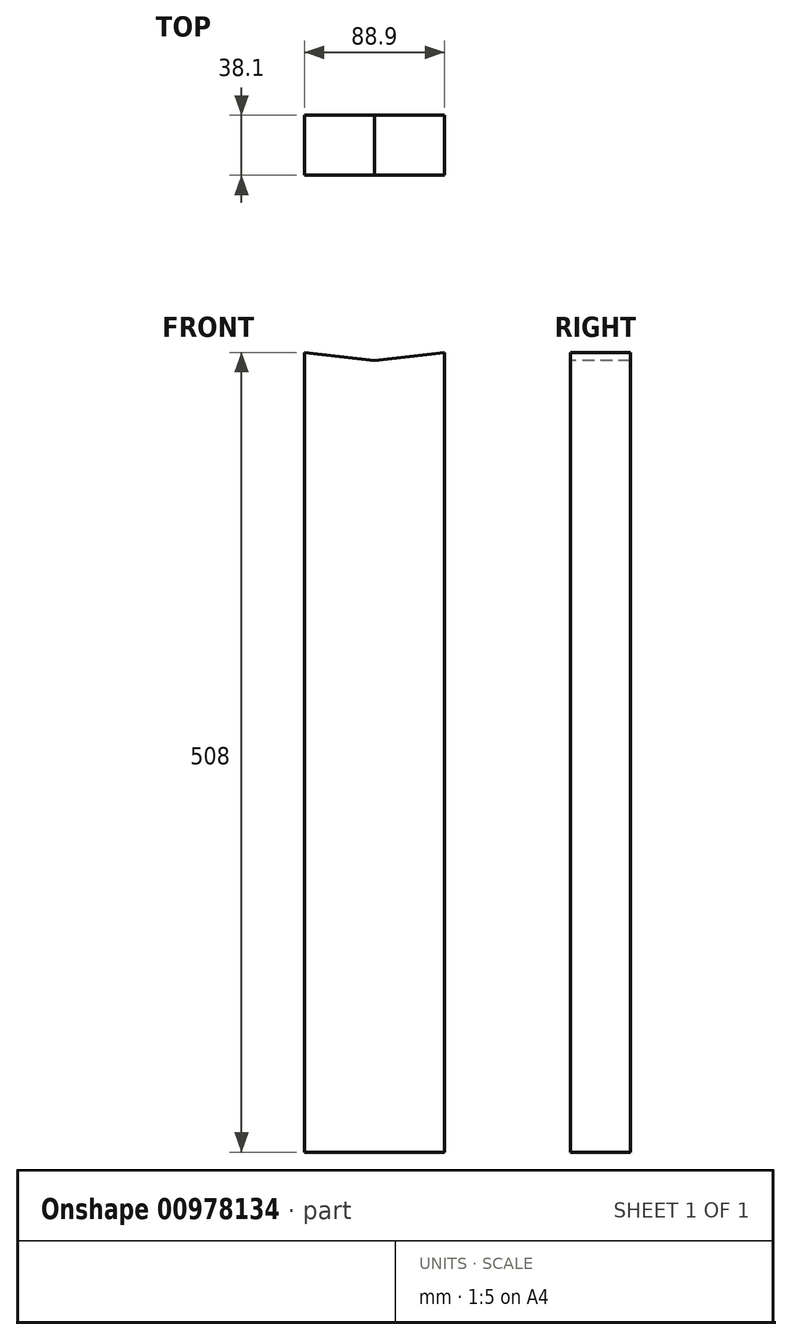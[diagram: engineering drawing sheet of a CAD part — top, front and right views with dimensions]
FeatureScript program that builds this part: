
annotation { "Feature Type Name" : "Feature", "Feature Type Description" : "" }
export const myFeature = defineFeature(function(context is Context, id is Id, definition is map)
    precondition{}
    {
        {
            var Q0;
            Q0=qCreatedBy(makeId("Top.planeOp"),FACE);
            var sketch = newSketch(context, id + "F0", { "sketchPlane" : qUnion([Q0])});
            skLineSegment(sketch, "E0.bottom", {"start": v(0, 0) * mm, "end": v(88.9, 0) * mm});
            skLineSegment(sketch, "E0.top", {"start": v(0, 38.1) * mm, "end": v(88.9, 38.1) * mm});
            skLineSegment(sketch, "E0.left", {"start": v(0, 0) * mm, "end": v(0, 38.1) * mm});
            skLineSegment(sketch, "E0.right", {"start": v(88.9, 0) * mm, "end": v(88.9, 38.1) * mm});
            skSolve(sketch);
        }
        {
            var Q0;
            Q0=makeQuery(id+"F0.imprint","IMPRINT",FACE,{"disambiguationData":[TD([[makeQuery(id+"F0.imprint","IMPRINT",EDGE,{"derivedFrom":sQuery(id+"F0.wireOp",EDGE,"E0.bottom")}),1.0]])]});
            extrude(context, id + "F1", {"entities" : qUnion([Q0]), "depth" : 508 * mm, "offsetDistance" : 25.4 * mm});
        }
        {
            var Q0;
            Q0=makeQuery(id+"F1.opExtrude","SWEPT_FACE",FACE,{"disambiguationData":[OSD([sQuery(id+"F0.wireOp",EDGE,"E0.bottom")])]});
            var sketch = newSketch(context, id + "F2", { "sketchPlane" : qUnion([Q0])});
            skLineSegment(sketch, "E1", {"start": v(0, 508) * mm, "end": v(44.45, 502.92) * mm});
            skLineSegment(sketch, "E2", {"start": v(44.45, 502.92) * mm, "end": v(88.9, 508) * mm});
            skLineSegment(sketch, "E3", {"start": v(88.9, 508) * mm, "end": v(0, 508) * mm});
            skSolve(sketch);
        }
        {
            var Q0;
            Q0=makeQuery(id+"F2.imprint","IMPRINT",FACE,{"disambiguationData":[TD([[makeQuery(id+"F2.imprint","IMPRINT",EDGE,{"derivedFrom":sQuery(id+"F2.wireOp",EDGE,"E1")}),1.0]])]});
            extrude(context, id + "F3", {"entities" : qUnion([Q0]), "operationType" : NewBodyOperationType.REMOVE, "endBound" : BoundingType.UP_TO_NEXT, "oppositeDirection" : true, "depth" : 25.4 * mm, "offsetDistance" : 25.4 * mm});
        }
    });
